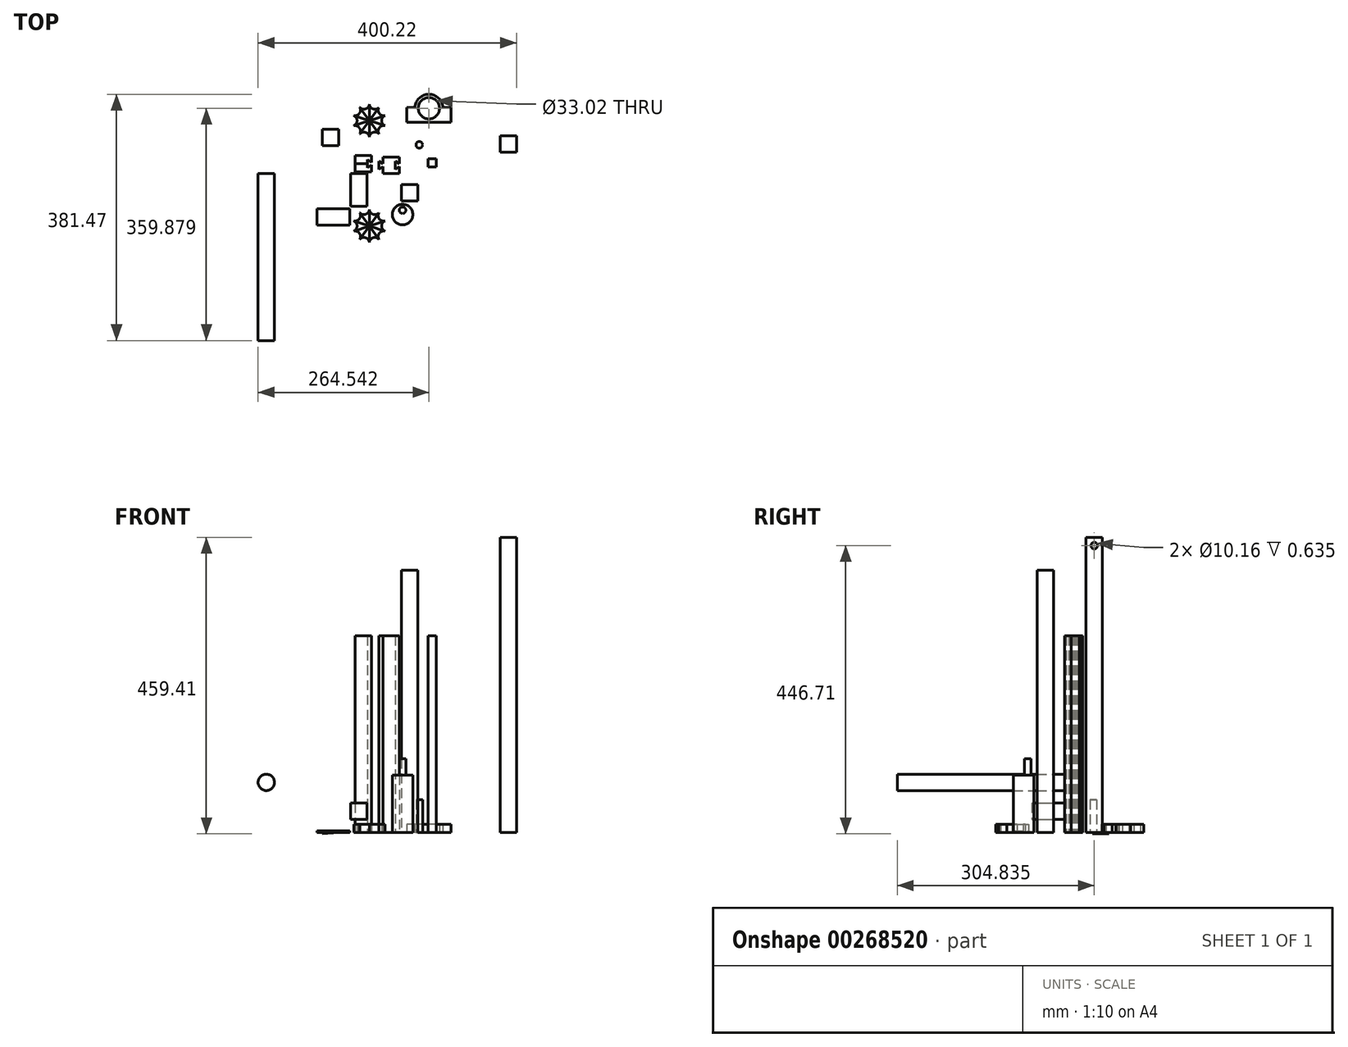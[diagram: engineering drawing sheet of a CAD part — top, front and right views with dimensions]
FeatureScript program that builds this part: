
annotation { "Feature Type Name" : "Feature", "Feature Type Description" : "" }
export const myFeature = defineFeature(function(context is Context, id is Id, definition is map)
    precondition{}
    {
        {
            var Q0;
            Q0=qCreatedBy(makeId("Top.planeOp"),FACE);
            var sketch = newSketch(context, id + "F0", { "sketchPlane" : qUnion([Q0])});
            skLineSegment(sketch, "E0", {"start": v(0, 0) * mm, "end": v(12.7, 0) * mm});
            skLineSegment(sketch, "E1", {"start": v(0, 0) * mm, "end": v(-6.35, 0) * mm});
            skLineSegment(sketch, "E2", {"start": v(12.7, 12.7) * mm, "end": v(-12.7, 12.7) * mm});
            skLineSegment(sketch, "E3", {"start": v(-12.7, 12.7) * mm, "end": v(-12.7, 6.35) * mm});
            skLineSegment(sketch, "E4", {"start": v(-12.7, 6.35) * mm, "end": v(-6.35, 10.67) * mm});
            skLineSegment(sketch, "E5", {"start": v(-6.35, 10.67) * mm, "end": v(-6.35, 0) * mm});
            skLineSegment(sketch, "E6", {"start": v(12.7, 0) * mm, "end": v(19.05, 0) * mm});
            skLineSegment(sketch, "E7", {"start": v(19.05, 0) * mm, "end": v(19.05, 10.67) * mm});
            skLineSegment(sketch, "E8", {"start": v(19.05, 10.67) * mm, "end": v(12.7, 6.35) * mm});
            skLineSegment(sketch, "E9", {"start": v(12.7, 6.35) * mm, "end": v(12.7, 0) * mm});
            skLineSegment(sketch, "E10", {"start": v(12.7, 6.35) * mm, "end": v(12.7, 12.7) * mm});
            skSolve(sketch);
        }
        {
            var Q0;
            Q0 = qSketchRegion(id + "F0", true);
            extrude(context, id + "F1", {"entities" : qUnion([Q0]), "depth" : 304.8 * mm});
        }
        {
            var Q0;
            Q0=makeQuery(id+"F1.opExtrude","SWEPT_BODY",BODY,{"disambiguationData":[OSD([sQuery(id+"F0.wireOp",EDGE,"E0"),sQuery(id+"F0.wireOp",EDGE,"E1"),sQuery(id+"F0.wireOp",EDGE,"YjheBlJf-i1gA-wtiC-qzgj-DnNIA5xnJrwv"),sQuery(id+"F0.wireOp",EDGE,"E2"),sQuery(id+"F0.wireOp",EDGE,"E3"),sQuery(id+"F0.wireOp",EDGE,"E4"),sQuery(id+"F0.wireOp",EDGE,"E5"),sQuery(id+"F0.wireOp",EDGE,"E6"),sQuery(id+"F0.wireOp",EDGE,"E7"),sQuery(id+"F0.wireOp",EDGE,"E8")])]});
            var Q1;
            Q1=makeQuery(id+"F1.opExtrude","SWEPT_FACE",FACE,{"disambiguationData":[OSD([sQuery(id+"F0.wireOp",EDGE,"E2")])]});
            mirror(context, id + "F2", {"operationType" : NewBodyOperationType.ADD, "entities" : qUnion([Q0]), "mirrorPlane" : qUnion([Q1])});
        }
        {
            var Q0;
            Q0=qCreatedBy(makeId("Top.planeOp"),FACE);
            var sketch = newSketch(context, id + "F3", { "sketchPlane" : qUnion([Q0])});
            skLineSegment(sketch, "E11.bottom", {"start": v(-108.64, -80.54) * mm, "end": v(-57.84, -80.54) * mm});
            skLineSegment(sketch, "E11.top", {"start": v(-108.64, -55.14) * mm, "end": v(-57.84, -55.14) * mm});
            skLineSegment(sketch, "E11.left", {"start": v(-108.64, -80.54) * mm, "end": v(-108.64, -55.14) * mm});
            skLineSegment(sketch, "E11.right", {"start": v(-57.84, -80.54) * mm, "end": v(-57.84, -55.14) * mm});
            skSolve(sketch);
        }
        {
            var Q0;
            Q0 = qSketchRegion(id + "F3", true);
            extrude(context, id + "F4", {"entities" : qUnion([Q0]), "depth" : 2.54 * mm});
        }
        {
            var Q0;
            Q0=qCreatedBy(makeId("Front.planeOp"),FACE);
            var sketch = newSketch(context, id + "F5", { "sketchPlane" : qUnion([Q0])});
            skLineSegment(sketch, "E12.bottom", {"start": v(-56.3, 45.52) * mm, "end": v(-30.9, 45.52) * mm});
            skLineSegment(sketch, "E12.top", {"start": v(-56.3, 20.12) * mm, "end": v(-30.9, 20.12) * mm});
            skLineSegment(sketch, "E12.left", {"start": v(-56.3, 45.52) * mm, "end": v(-56.3, 20.12) * mm});
            skLineSegment(sketch, "E12.right", {"start": v(-30.9, 45.52) * mm, "end": v(-30.9, 20.12) * mm});
            skSolve(sketch);
        }
        {
            var Q0;
            Q0 = qSketchRegion(id + "F5", true);
            extrude(context, id + "F6", {"entities" : qUnion([Q0]), "depth" : 50.8 * mm});
        }
        {
            var Q0;
            Q0=qCreatedBy(makeId("Front.planeOp"),FACE);
            var sketch = newSketch(context, id + "F7", { "sketchPlane" : qUnion([Q0])});
            skCircle(sketch, "E13", {"center": v(-186.9, 77.6) * mm, "radius": 12.7 * mm});
            skSolve(sketch);
        }
        {
            var Q0;
            Q0 = qSketchRegion(id + "F7", true);
            extrude(context, id + "F8", {"entities" : qUnion([Q0]), "depth" : 259.08 * mm});
        }
        {
            var Q0;
            Q0=qCreatedBy(makeId("Top.planeOp"),FACE);
            var sketch = newSketch(context, id + "F9", { "sketchPlane" : qUnion([Q0])});
            skLineSegment(sketch, "E14", {"start": v(-23.95, 27.6) * mm, "end": v(-36.65, 27.6) * mm});
            skLineSegment(sketch, "E15", {"start": v(-23.95, 27.6) * mm, "end": v(-23.95, 16.92) * mm});
            skLineSegment(sketch, "E16", {"start": v(-30.3, 27.6) * mm, "end": v(-30.3, 21.24) * mm});
            skLineSegment(sketch, "E17", {"start": v(-30.3, 21.24) * mm, "end": v(-23.95, 16.92) * mm});
            skLineSegment(sketch, "E18", {"start": v(-30.3, 21.24) * mm, "end": v(-30.3, 14.9) * mm});
            skLineSegment(sketch, "E19", {"start": v(-36.65, 27.6) * mm, "end": v(-36.65, 14.9) * mm});
            skLineSegment(sketch, "E20", {"start": v(-36.65, 14.9) * mm, "end": v(-30.3, 14.9) * mm});
            skLineSegment(sketch, "E21", {"start": v(-36.65, 27.6) * mm, "end": v(-49.35, 27.6) * mm});
            skLineSegment(sketch, "E22", {"start": v(-49.35, 27.6) * mm, "end": v(-49.35, 14.9) * mm});
            skLineSegment(sketch, "E23", {"start": v(-49.35, 14.9) * mm, "end": v(-36.65, 14.9) * mm});
            skSolve(sketch);
        }
        {
            var Q0;
            Q0 = qSketchRegion(id + "F9", true);
            extrude(context, id + "F10", {"entities" : qUnion([Q0]), "depth" : 304.8 * mm});
        }
        {
            var Q0;
            Q0=makeQuery(id+"F10.opExtrude","SWEPT_BODY",BODY,{"disambiguationData":[OSD([sQuery(id+"F9.wireOp",EDGE,"E14"),sQuery(id+"F9.wireOp",EDGE,"E15"),sQuery(id+"F9.wireOp",EDGE,"E17"),sQuery(id+"F9.wireOp",EDGE,"E18"),sQuery(id+"F9.wireOp",EDGE,"E19"),sQuery(id+"F9.wireOp",EDGE,"E20")])]});
            var Q1;
            Q1=makeQuery(id+"F10.opExtrude","SWEPT_FACE",FACE,{"disambiguationData":[OSD([sQuery(id+"F9.wireOp",EDGE,"E20")])]});
            mirror(context, id + "F11", {"operationType" : NewBodyOperationType.ADD, "entities" : qUnion([Q0]), "mirrorPlane" : qUnion([Q1])});
        }
        {
            var Q0;
            Q0=qCreatedBy(makeId("Top.planeOp"),FACE);
            var sketch = newSketch(context, id + "F12", { "sketchPlane" : qUnion([Q0])});
            skLineSegment(sketch, "E24.bottom", {"start": v(-100.47, 68.54) * mm, "end": v(-75.07, 68.54) * mm});
            skLineSegment(sketch, "E24.top", {"start": v(-100.47, 43.14) * mm, "end": v(-75.07, 43.14) * mm});
            skLineSegment(sketch, "E24.left", {"start": v(-100.47, 68.54) * mm, "end": v(-100.47, 43.14) * mm});
            skLineSegment(sketch, "E24.right", {"start": v(-75.07, 68.54) * mm, "end": v(-75.07, 43.14) * mm});
            skSolve(sketch);
        }
        {
            var Q0;
            Q0 = qSketchRegion(id + "F12", true);
            var Q1;
            Q1=sQuery(id+"F12.wireOp",EDGE,"E24.right");
            revolve(context, id + "F13", {"entities" : qUnion([Q0]), "axis" : qUnion([Q1]), "revolveType" : RevolveType.ONE_DIRECTION, "angle" : 5 * degree});
        }
        {
            var Q0;
            Q0=qCreatedBy(makeId("Top.planeOp"),FACE);
            var sketch = newSketch(context, id + "F14", { "sketchPlane" : qUnion([Q0])});
            skLineSegment(sketch, "E25.bottom", {"start": v(22.25, -17.36) * mm, "end": v(47.65, -17.36) * mm});
            skLineSegment(sketch, "E25.top", {"start": v(22.25, -42.76) * mm, "end": v(47.65, -42.76) * mm});
            skLineSegment(sketch, "E25.left", {"start": v(22.25, -17.36) * mm, "end": v(22.25, -42.76) * mm});
            skLineSegment(sketch, "E25.right", {"start": v(47.65, -17.36) * mm, "end": v(47.65, -42.76) * mm});
            skSolve(sketch);
        }
        {
            var Q0;
            Q0 = qSketchRegion(id + "F14", true);
            extrude(context, id + "F15", {"entities" : qUnion([Q0]), "depth" : 406.4 * mm});
        }
        {
            var Q0;
            Q0=qCreatedBy(makeId("Top.planeOp"),FACE);
            var sketch = newSketch(context, id + "F16", { "sketchPlane" : qUnion([Q0])});
            skCircle(sketch, "E26", {"center": v(24.15, -63.9) * mm, "radius": 15.88 * mm});
            skSolve(sketch);
        }
        {
            var Q0;
            Q0 = qSketchRegion(id + "F16", true);
            extrude(context, id + "F17", {"entities" : qUnion([Q0]), "depth" : 88.9 * mm});
        }
        {
            var Q0;
            Q0=makeQuery(id+"F17.opExtrude","CAP_FACE",FACE,{"disambiguationData":[OSD([sQuery(id+"F16.wireOp",EDGE,"E26")])],"isStart":false});
            var sketch = newSketch(context, id + "F18", { "sketchPlane" : qUnion([Q0])});
            skCircle(sketch, "E27", {"center": v(24.17, -57.13) * mm, "radius": 5.08 * mm});
            skSolve(sketch);
        }
        {
            var Q0;
            Q0 = qSketchRegion(id + "F18", true);
            extrude(context, id + "F19", {"entities" : qUnion([Q0]), "operationType" : NewBodyOperationType.ADD, "depth" : 25.4 * mm});
        }
        {
            var Q0;
            Q0=qCreatedBy(makeId("Top.planeOp"),FACE);
            var sketch = newSketch(context, id + "F20", { "sketchPlane" : qUnion([Q0])});
            skCircle(sketch, "E28", {"center": v(50, 44.16) * mm, "radius": 5.08 * mm});
            skSolve(sketch);
        }
        {
            var Q0;
            Q0 = qSketchRegion(id + "F20", true);
            extrude(context, id + "F21", {"entities" : qUnion([Q0]), "depth" : 50.8 * mm});
        }
        {
            var Q0;
            Q0=qCreatedBy(makeId("Top.planeOp"),FACE);
            var sketch = newSketch(context, id + "F22", { "sketchPlane" : qUnion([Q0])});
            skCircle(sketch, "E29", {"center": v(64.93, 100.8) * mm, "radius": 16.51 * mm});
            skArc(sketch, "E30", {"start": v(86.49, 102) * mm, "mid": v(64.93, 122.39) * mm, "end": v(43.38, 102) * mm});
            skLineSegment(sketch, "E31.top", {"start": v(43.38, 79.15) * mm, "end": v(86.56, 79.15) * mm});
            skLineSegment(sketch, "E32.trimOffspring", {"start": v(86.49, 102) * mm, "end": v(86.56, 102) * mm});
            skLineSegment(sketch, "E33.bottom", {"start": v(86.56, 102) * mm, "end": v(99.26, 102) * mm});
            skLineSegment(sketch, "E33.top", {"start": v(86.56, 79.15) * mm, "end": v(99.26, 79.15) * mm});
            skLineSegment(sketch, "E33.right", {"start": v(99.26, 102) * mm, "end": v(99.26, 79.15) * mm});
            skLineSegment(sketch, "E34.bottom", {"start": v(43.38, 102) * mm, "end": v(30.68, 102) * mm});
            skLineSegment(sketch, "E34.top", {"start": v(43.38, 79.15) * mm, "end": v(30.68, 79.15) * mm});
            skLineSegment(sketch, "E34.right", {"start": v(30.68, 102) * mm, "end": v(30.68, 79.15) * mm});
            skSolve(sketch);
        }
        {
            var Q0;
            Q0 = qSketchRegion(id + "F22", true);
            extrude(context, id + "F23", {"entities" : qUnion([Q0]), "depth" : 12.7 * mm});
        }
        {
            var Q0;
            Q0=qCreatedBy(makeId("Top.planeOp"),FACE);
            var sketch = newSketch(context, id + "F24", { "sketchPlane" : qUnion([Q0])});
            skLineSegment(sketch, "E35", {"start": v(-27.35, 81.64) * mm, "end": v(-27.35, 107.04) * mm});
            skLineSegment(sketch, "E36", {"start": v(-27.35, 81.64) * mm, "end": v(-42.28, 102.2) * mm});
            skLineSegment(sketch, "E37", {"start": v(-27.35, 81.64) * mm, "end": v(-33.23, 99.76) * mm});
            skArc(sketch, "E38", {"start": v(-42.28, 102.2) * mm, "mid": v(-33.23, 99.76) * mm, "end": v(-27.35, 107.04) * mm});
            skSolve(sketch);
        }
        {
            var Q0;
            Q0 = qSketchRegion(id + "F24", true);
            extrude(context, id + "F25", {"entities" : qUnion([Q0]), "depth" : 12.7 * mm});
        }
        {
            var Q0;
            Q0=makeQuery(id+"F25.opExtrude","SWEPT_BODY",BODY,{"disambiguationData":[OSD([sQuery(id+"F24.wireOp",EDGE,"E35"),sQuery(id+"F24.wireOp",EDGE,"E36"),sQuery(id+"F24.wireOp",EDGE,"E38")])]});
            var Q1;
            Q1=makeQuery(id+"F25.opExtrude","SWEPT_EDGE",EDGE,{"disambiguationData":[OSD([sQuery(id+"F24.wireOp",EDGE,"E35"),sQuery(id+"F24.wireOp",EDGE,"E36"),sQuery(id+"F24.wireOp",EDGE,"E37")])]});
            circularPattern(context, id + "F26", {"entities" : qUnion([Q0]), "axis" : qUnion([Q1]), "angle" : 360 * degree, "instanceCount" : 10, "equalSpace" : true});
        }
        {
            var Q0;
            Q0=makeQuery(id+"F26.opPattern","COPY",BODY,{"derivedFrom":makeQuery(id+"F25.opExtrude","SWEPT_BODY",BODY,{"disambiguationData":[OSD([sQuery(id+"F24.wireOp",EDGE,"E35"),sQuery(id+"F24.wireOp",EDGE,"E36"),sQuery(id+"F24.wireOp",EDGE,"E38")])]}),"instanceName":"2"});
            var Q1;
            Q1=makeQuery(id+"F26.opPattern","COPY",BODY,{"derivedFrom":makeQuery(id+"F25.opExtrude","SWEPT_BODY",BODY,{"disambiguationData":[OSD([sQuery(id+"F24.wireOp",EDGE,"E35"),sQuery(id+"F24.wireOp",EDGE,"E36"),sQuery(id+"F24.wireOp",EDGE,"E38")])]}),"instanceName":"8"});
            var Q2;
            Q2=makeQuery(id+"F26.opPattern","COPY",BODY,{"derivedFrom":makeQuery(id+"F25.opExtrude","SWEPT_BODY",BODY,{"disambiguationData":[OSD([sQuery(id+"F24.wireOp",EDGE,"E35"),sQuery(id+"F24.wireOp",EDGE,"E36"),sQuery(id+"F24.wireOp",EDGE,"E38")])]}),"instanceName":"9"});
            var Q3;
            Q3=makeQuery(id+"F26.opPattern","COPY",BODY,{"derivedFrom":makeQuery(id+"F25.opExtrude","SWEPT_BODY",BODY,{"disambiguationData":[OSD([sQuery(id+"F24.wireOp",EDGE,"E35"),sQuery(id+"F24.wireOp",EDGE,"E36"),sQuery(id+"F24.wireOp",EDGE,"E38")])]}),"instanceName":"4"});
            var Q4;
            Q4=makeQuery(id+"F26.opPattern","COPY",BODY,{"derivedFrom":makeQuery(id+"F25.opExtrude","SWEPT_BODY",BODY,{"disambiguationData":[OSD([sQuery(id+"F24.wireOp",EDGE,"E35"),sQuery(id+"F24.wireOp",EDGE,"E36"),sQuery(id+"F24.wireOp",EDGE,"E38")])]}),"instanceName":"3"});
            var Q5;
            Q5=makeQuery(id+"F26.opPattern","COPY",BODY,{"derivedFrom":makeQuery(id+"F25.opExtrude","SWEPT_BODY",BODY,{"disambiguationData":[OSD([sQuery(id+"F24.wireOp",EDGE,"E35"),sQuery(id+"F24.wireOp",EDGE,"E36"),sQuery(id+"F24.wireOp",EDGE,"E38")])]}),"instanceName":"1"});
            var Q6;
            Q6=makeQuery(id+"F25.opExtrude","SWEPT_BODY",BODY,{"disambiguationData":[OSD([sQuery(id+"F24.wireOp",EDGE,"E35"),sQuery(id+"F24.wireOp",EDGE,"E36"),sQuery(id+"F24.wireOp",EDGE,"E38")])]});
            var Q7;
            Q7=makeQuery(id+"F26.opPattern","COPY",BODY,{"derivedFrom":makeQuery(id+"F25.opExtrude","SWEPT_BODY",BODY,{"disambiguationData":[OSD([sQuery(id+"F24.wireOp",EDGE,"E35"),sQuery(id+"F24.wireOp",EDGE,"E36"),sQuery(id+"F24.wireOp",EDGE,"E38")])]}),"instanceName":"7"});
            var Q8;
            Q8=makeQuery(id+"F26.opPattern","COPY",BODY,{"derivedFrom":makeQuery(id+"F25.opExtrude","SWEPT_BODY",BODY,{"disambiguationData":[OSD([sQuery(id+"F24.wireOp",EDGE,"E35"),sQuery(id+"F24.wireOp",EDGE,"E36"),sQuery(id+"F24.wireOp",EDGE,"E38")])]}),"instanceName":"6"});
            var Q9;
            Q9=makeQuery(id+"F26.opPattern","COPY",BODY,{"derivedFrom":makeQuery(id+"F25.opExtrude","SWEPT_BODY",BODY,{"disambiguationData":[OSD([sQuery(id+"F24.wireOp",EDGE,"E35"),sQuery(id+"F24.wireOp",EDGE,"E36"),sQuery(id+"F24.wireOp",EDGE,"E38")])]}),"instanceName":"5"});
            var Q10;
            Q10=qCreatedBy(makeId("Front.planeOp"),FACE);
            mirror(context, id + "F27", {"operationType" : NewBodyOperationType.ADD, "entities" : qUnion([Q0, Q1, Q2, Q3, Q4, Q5, Q6, Q7, Q8, Q9]), "mirrorPlane" : qUnion([Q10])});
        }
        {
            var Q0;
            Q0=qCreatedBy(makeId("Top.planeOp"),FACE);
            var sketch = newSketch(context, id + "F28", { "sketchPlane" : qUnion([Q0])});
            skLineSegment(sketch, "E39.bottom", {"start": v(200.61, 33.06) * mm, "end": v(175.21, 33.06) * mm});
            skLineSegment(sketch, "E39.top", {"start": v(200.61, 58.46) * mm, "end": v(175.21, 58.46) * mm});
            skLineSegment(sketch, "E39.left", {"start": v(200.61, 33.06) * mm, "end": v(200.61, 58.46) * mm});
            skLineSegment(sketch, "E39.right", {"start": v(175.21, 33.06) * mm, "end": v(175.21, 58.46) * mm});
            skSolve(sketch);
        }
        {
            var Q0;
            Q0 = qSketchRegion(id + "F28", true);
            extrude(context, id + "F29", {"entities" : qUnion([Q0]), "depth" : 457.2 * mm});
        }
        {
            var Q0;
            Q0=qCreatedBy(makeId("Top.planeOp"),FACE);
            var sketch = newSketch(context, id + "F30", { "sketchPlane" : qUnion([Q0])});
            skLineSegment(sketch, "E40.bottom", {"start": v(63.38, 22.73) * mm, "end": v(76.08, 22.73) * mm});
            skLineSegment(sketch, "E40.top", {"start": v(63.38, 10.03) * mm, "end": v(76.08, 10.03) * mm});
            skLineSegment(sketch, "E40.left", {"start": v(63.38, 22.73) * mm, "end": v(63.38, 10.03) * mm});
            skLineSegment(sketch, "E40.right", {"start": v(76.08, 22.73) * mm, "end": v(76.08, 10.03) * mm});
            skSolve(sketch);
        }
        {
            var Q0;
            Q0 = qSketchRegion(id + "F30", true);
            extrude(context, id + "F31", {"entities" : qUnion([Q0]), "depth" : 304.8 * mm});
        }
        {
            var Q0;
            Q0=makeQuery(id+"F29.opExtrude","SWEPT_FACE",FACE,{"disambiguationData":[OSD([sQuery(id+"F28.wireOp",EDGE,"E39.left")])]});
            var sketch = newSketch(context, id + "F32", { "sketchPlane" : qUnion([Q0])});
            skCircle(sketch, "E41", {"center": v(45.76, 444.5) * mm, "radius": 5.08 * mm});
            skPoint(sketch, "E42.right.end.orphan", {"position": v(58.46, 431.8) * mm});
            skPoint(sketch, "E42.bottom.start.orphan", {"position": v(33.06, 457.2) * mm});
            skSolve(sketch);
        }
        {
            var Q0;
            Q0 = qSketchRegion(id + "F32", true);
            extrude(context, id + "F33", {"entities" : qUnion([Q0]), "operationType" : NewBodyOperationType.REMOVE, "oppositeDirection" : true, "depth" : 0.64 * mm});
        }
        {
            var Q0;
            Q0=makeQuery(id+"F29.opExtrude","SWEPT_FACE",FACE,{"disambiguationData":[OSD([sQuery(id+"F28.wireOp",EDGE,"E39.right")])]});
            var sketch = newSketch(context, id + "F34", { "sketchPlane" : qUnion([Q0])});
            skCircle(sketch, "E43", {"center": v(-45.76, 444.5) * mm, "radius": 5.08 * mm});
            skPoint(sketch, "E44.top.start.orphan", {"position": v(-58.46, 431.8) * mm});
            skPoint(sketch, "E44.right.start.orphan", {"position": v(-33.06, 457.2) * mm});
            skSolve(sketch);
        }
        {
            var Q0;
            Q0=makeQuery(id+"F34.imprint","IMPRINT",FACE,{"disambiguationData":[TD([[makeQuery(id+"F34.imprint","IMPRINT",EDGE,{"derivedFrom":sQuery(id+"F34.wireOp",EDGE,"E43")}),1.0]])]});
            extrude(context, id + "F35", {"entities" : qUnion([Q0]), "operationType" : NewBodyOperationType.REMOVE, "oppositeDirection" : true, "depth" : 0.64 * mm});
        }
    });
